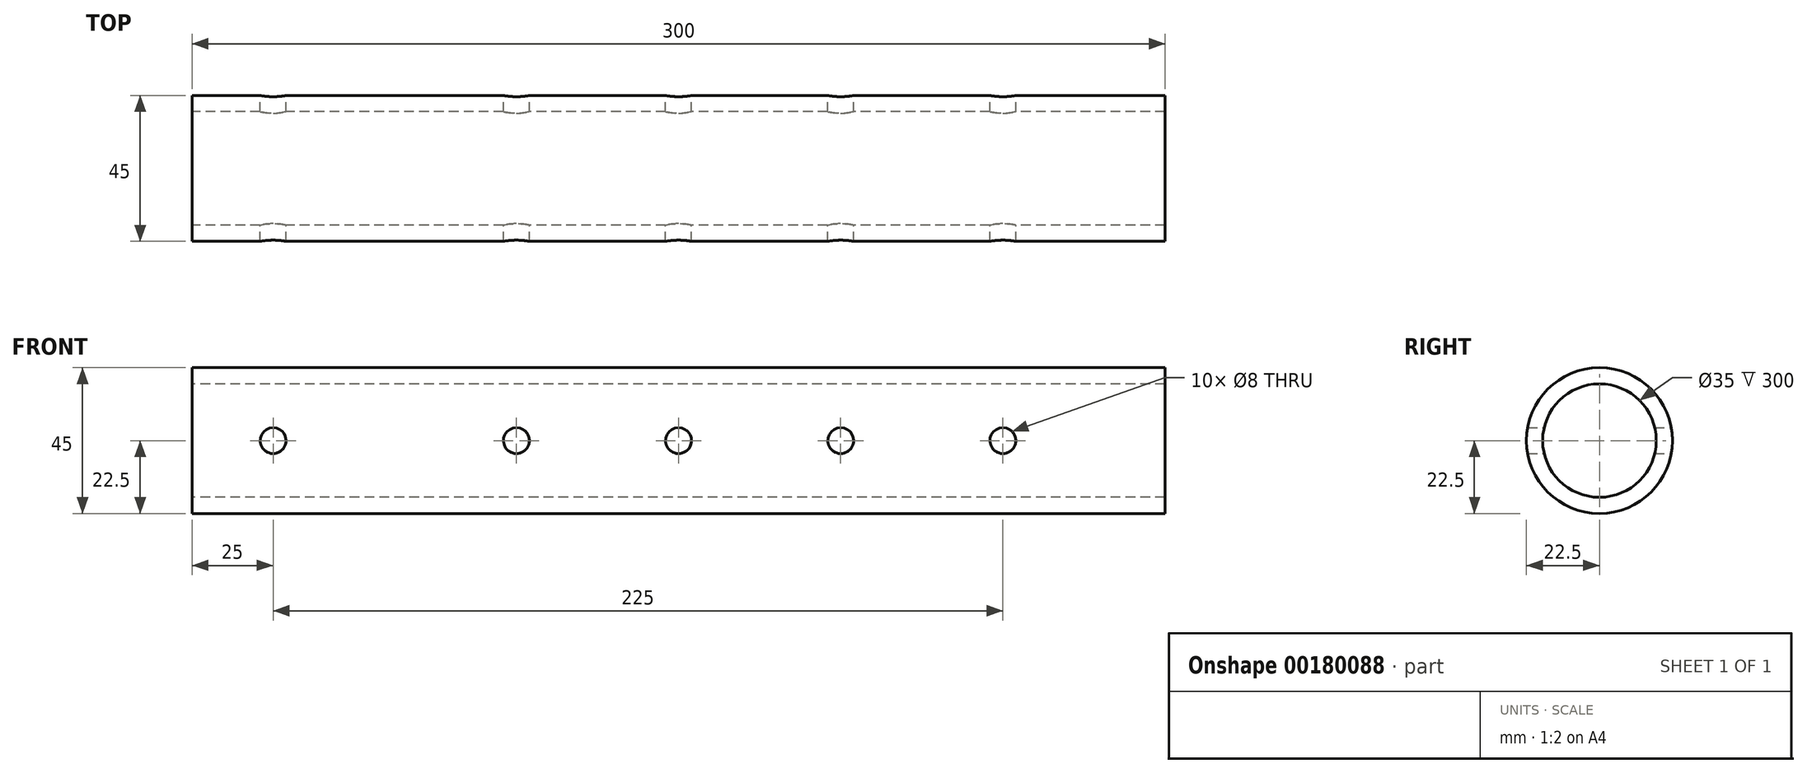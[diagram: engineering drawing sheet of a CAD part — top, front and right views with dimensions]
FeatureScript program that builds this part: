
annotation { "Feature Type Name" : "Feature", "Feature Type Description" : "" }
export const myFeature = defineFeature(function(context is Context, id is Id, definition is map)
    precondition{}
    {
        {
            var Q0;
            Q0=qCreatedBy(makeId("Right.planeOp"),FACE);
            var sketch = newSketch(context, id + "F0", { "sketchPlane" : qUnion([Q0])});
            skCircle(sketch, "E0", {"center": v(0, 0) * mm, "radius": 22.5 * mm});
            skCircle(sketch, "E1", {"center": v(0, 0) * mm, "radius": 17.5 * mm});
            skSolve(sketch);
        }
        {
            var Q0;
            Q0=makeQuery(id+"F0.imprint","IMPRINT",FACE,{"disambiguationData":[TD([[makeQuery(id+"F0.imprint","IMPRINT",EDGE,{"derivedFrom":sQuery(id+"F0.wireOp",EDGE,"E0")}),1.0]])]});
            extrude(context, id + "F1", {"entities" : qUnion([Q0]), "depth" : 300 * mm});
        }
        {
            var Q0;
            Q0=qCreatedBy(makeId("Front.planeOp"),FACE);
            var sketch = newSketch(context, id + "F2", { "sketchPlane" : qUnion([Q0])});
            skCircle(sketch, "E2", {"center": v(25, 0) * mm, "radius": 4 * mm});
            skSolve(sketch);
        }
        {
            var Q0;
            Q0 = qSketchRegion(id + "F2", true);
            extrude(context, id + "F3", {"entities" : qUnion([Q0]), "operationType" : NewBodyOperationType.REMOVE, "endBound" : BoundingType.SYMMETRIC, "depth" : 50 * mm});
        }
        {
            var Q0;
            Q0=qCreatedBy(makeId("Front.planeOp"),FACE);
            var sketch = newSketch(context, id + "F4", { "sketchPlane" : qUnion([Q0])});
            skCircle(sketch, "E3", {"center": v(100, 0) * mm, "radius": 4 * mm});
            skCircle(sketch, "E4.1.0.0", {"center": v(150, 0) * mm, "radius": 4 * mm});
            skCircle(sketch, "E4.2.0.0", {"center": v(200, 0) * mm, "radius": 4 * mm});
            skCircle(sketch, "E4.3.0.0", {"center": v(250, 0) * mm, "radius": 4 * mm});
            skLineSegment(sketch, "E4.direction1", {"start": v(100, 0) * mm, "end": v(150, 0) * mm, "construction": true});
            skSolve(sketch);
        }
        {
            var Q0;
            Q0 = qSketchRegion(id + "F4", true);
            extrude(context, id + "F5", {"entities" : qUnion([Q0]), "operationType" : NewBodyOperationType.REMOVE, "endBound" : BoundingType.SYMMETRIC, "depth" : 50 * mm});
        }
    });
